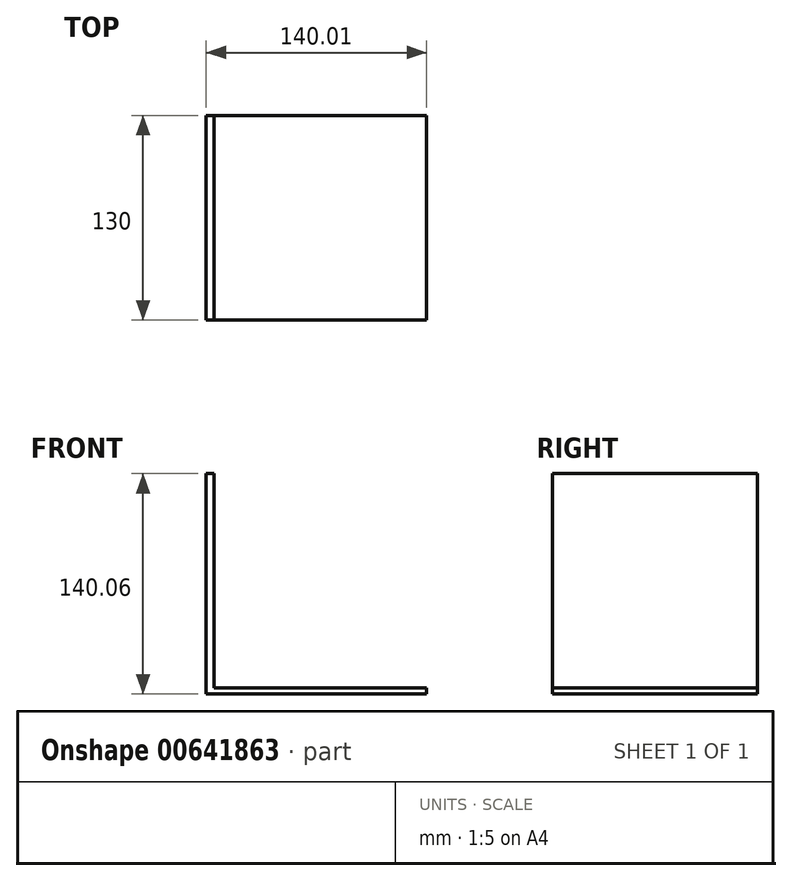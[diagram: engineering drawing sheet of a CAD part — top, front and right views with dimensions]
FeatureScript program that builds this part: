
annotation { "Feature Type Name" : "Feature", "Feature Type Description" : "" }
export const myFeature = defineFeature(function(context is Context, id is Id, definition is map)
    precondition{}
    {
        {
            var Q0;
            Q0=qCreatedBy(makeId("Front.planeOp"),FACE);
            var sketch = newSketch(context, id + "F0", { "sketchPlane" : qUnion([Q0])});
            skLineSegment(sketch, "E0", {"start": v(-104.04, -68.78) * mm, "end": v(35.96, -68.78) * mm});
            skLineSegment(sketch, "E1", {"start": v(-104.04, 71.22) * mm, "end": v(35.96, 71.22) * mm});
            skLineSegment(sketch, "E2.0", {"start": v(-104.04, -64.78) * mm, "end": v(35.96, -64.78) * mm});
            skLineSegment(sketch, "E3.0", {"start": v(-104.04, 67.22) * mm, "end": v(35.96, 67.22) * mm});
            skLineSegment(sketch, "E4", {"start": v(-104.04, -68.78) * mm, "end": v(-104.04, -64.78) * mm});
            skLineSegment(sketch, "E5", {"start": v(35.96, -68.78) * mm, "end": v(35.96, -64.78) * mm});
            skLineSegment(sketch, "E6", {"start": v(35.96, 67.22) * mm, "end": v(35.96, 71.22) * mm});
            skLineSegment(sketch, "E7", {"start": v(-104.04, 67.22) * mm, "end": v(-104.04, 71.22) * mm});
            skSolve(sketch);
        }
        {
            var Q0;
            Q0=qCreatedBy(makeId("Right.planeOp"),FACE);
            var sketch = newSketch(context, id + "F1", { "sketchPlane" : qUnion([Q0])});
            skLineSegment(sketch, "E8", {"start": v(0, -86.07) * mm, "end": v(-130, -86.07) * mm});
            skSolve(sketch);
        }
        {
            var Q0;
            Q0=qCreatedBy(makeId("Front.planeOp"),FACE);
            var sketch = newSketch(context, id + "F2", { "sketchPlane" : qUnion([Q0])});
            skLineSegment(sketch, "E9", {"start": v(-103.99, -68.85) * mm, "end": v(-104.05, 71.2) * mm});
            skLineSegment(sketch, "E10", {"start": v(36.04, -68.88) * mm, "end": v(35.97, 71.22) * mm});
            skLineSegment(sketch, "E11.0", {"start": v(-98.99, -68.85) * mm, "end": v(-99.05, 71.2) * mm});
            skLineSegment(sketch, "E12.0", {"start": v(31.04, -68.88) * mm, "end": v(30.97, 71.22) * mm});
            skLineSegment(sketch, "E13", {"start": v(-104.05, 71.2) * mm, "end": v(-99.05, 71.2) * mm});
            skLineSegment(sketch, "E14", {"start": v(-98.99, -68.85) * mm, "end": v(-103.99, -68.85) * mm});
            skLineSegment(sketch, "E15", {"start": v(31.04, -68.88) * mm, "end": v(36.04, -68.88) * mm});
            skLineSegment(sketch, "E16", {"start": v(30.97, 71.22) * mm, "end": v(35.97, 71.22) * mm});
            skSolve(sketch);
        }
        {
            var Q0;
            Q0=makeQuery(id+"F0.imprint","IMPRINT",FACE,{"disambiguationData":[TD([[makeQuery(id+"F0.imprint","IMPRINT",EDGE,{"derivedFrom":sQuery(id+"F0.wireOp",EDGE,"E0")}),1.0]])]});
            var Q1;
            Q1=sQuery(id+"F1.wireOp",EDGE,"E8");
            sweep(context, id + "F3", {"profiles" : qUnion([Q0]), "path" : qUnion([Q1])});
        }
        {
            var Q0;
            Q0=makeQuery(id+"F2.imprint","IMPRINT",FACE,{"disambiguationData":[TD([[makeQuery(id+"F2.imprint","IMPRINT",EDGE,{"derivedFrom":sQuery(id+"F2.wireOp",EDGE,"E9")}),-1.0]])]});
            var Q1;
            Q1=makeQuery(id+"F3.opSweep","SWEPT_EDGE",EDGE,{"disambiguationData":[OSD([sQuery(id+"F0.wireOp",EDGE,"E2.0"),sQuery(id+"F0.wireOp",EDGE,"E4"),sQuery(id+"F1.wireOp",EDGE,"E8")])]});
            sweep(context, id + "F4", {"operationType" : NewBodyOperationType.ADD, "profiles" : qUnion([Q0]), "path" : qUnion([Q1])});
        }
    });
